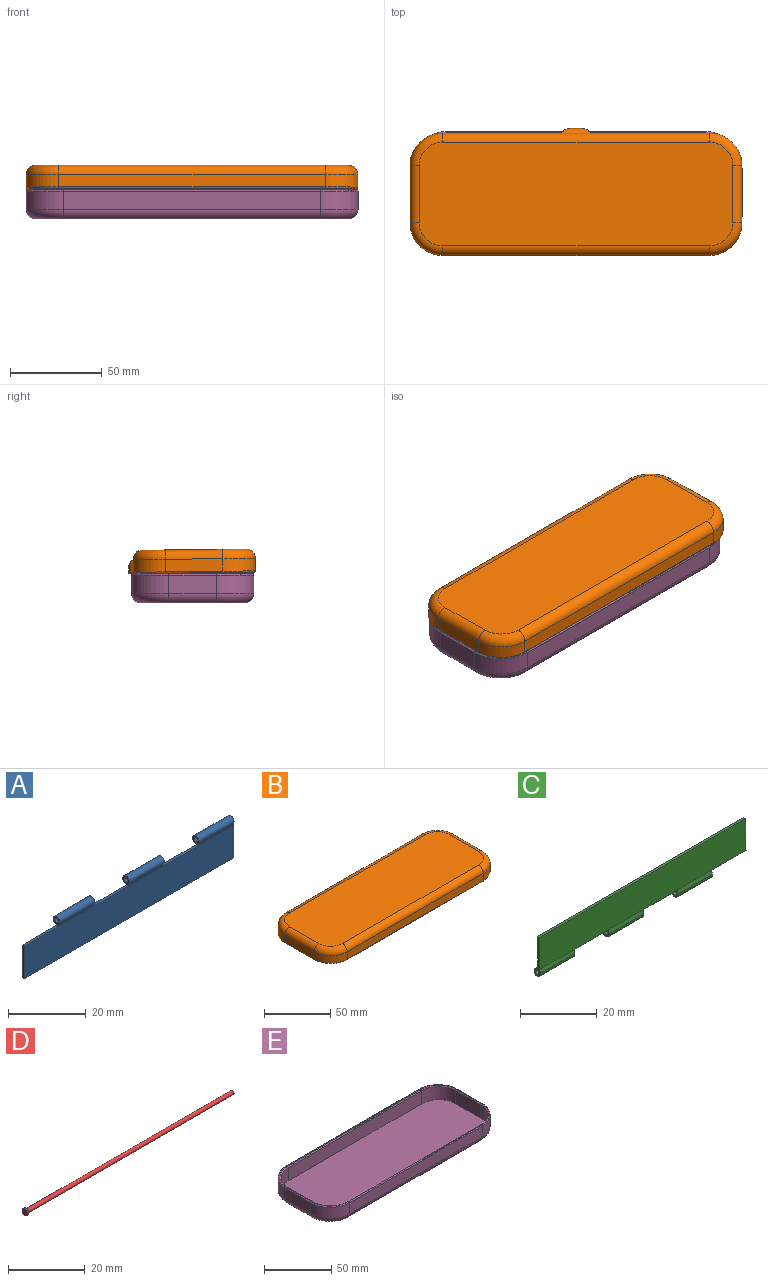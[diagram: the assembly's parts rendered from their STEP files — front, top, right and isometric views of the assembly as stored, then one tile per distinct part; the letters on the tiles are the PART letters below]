
ASSEMBLY  parts=5 mates=5
PART A: 25 faces, bbox 76.2x2.4x12.8 mm
  f0: cylinder r=1.21mm len=12.7mm, axis (-1,0,0), area 78.6mm2, adj f2,f6,f15,f16
  f1: cylinder r=1.21mm len=12.7mm, axis (-1,0,0), area 78.6mm2, adj f3,f5,f17,f18
  f2: plane 12.7x0.24mm, normal (0,0.94,0.33), area 3.3mm2, adj f0,f10,f15,f16
  f3: plane 12.7x0.24mm, normal (0,0.94,0.33), area 3.3mm2, adj f1,f10,f17,f18
  f4: plane 10.16x0.76mm, normal (-1,0,0), area 7.8mm2, adj f10,f11,f19,f24
  f5: plane 12.7x1.18mm, normal (0,-0.98,-0.2), area 15.3mm2, adj f1,f11,f17,f18
  f6: plane 12.7x1.18mm, normal (0,-0.98,-0.2), area 15.3mm2, adj f0,f11,f15,f16
  f7: plane 12.7x1.18mm, normal (0,-0.98,-0.2), area 15.3mm2, adj f8,f11,f13,f14
  f8: cylinder r=1.21mm len=12.7mm, axis (-1,0,0), area 78.6mm2, adj f7,f9,f13,f14
  f9: plane 12.7x0.24mm, normal (0,0.94,0.33), area 3.3mm2, adj f8,f10,f13,f14
  f10: plane 76.2x10.16mm, normal (0,1,0), area 774.2mm2, adj f2,f3,f4,f9,f13,f19,f20,f21
  f11: plane 76.2x10.16mm, normal (0,-1,0), area 774.2mm2, adj f4,f5,f6,f7,f13,f19,f20,f21
  f12: cylinder r=0.64mm len=12.7mm, axis (-1,0,0), area 50.7mm2, adj f13,f14
  f13: plane 12.79x2.41mm, normal (1,0,0), area 11.4mm2, adj f7,f8,f9,f10,f11,f12,f24
  f14: plane 2.63x2.41mm, normal (-1,0,0), area 3.7mm2, adj f7,f8,f9,f12,f21
  f15: plane 2.63x2.41mm, normal (1,0,0), area 3.7mm2, adj f0,f2,f6,f21,f23
  f16: plane 2.63x2.41mm, normal (-1,0,0), area 3.7mm2, adj f0,f2,f6,f20,f23
  f17: plane 2.63x2.41mm, normal (1,0,0), area 3.7mm2, adj f1,f3,f5,f20,f22
  f18: plane 2.63x2.41mm, normal (-1,0,0), area 3.7mm2, adj f1,f3,f5,f19,f22
  f19: plane 12.7x0.76mm, normal (0,0,1), area 9.7mm2, adj f4,f10,f11,f18
  f20: plane 12.7x0.76mm, normal (0,0,1), area 9.7mm2, adj f10,f11,f16,f17
  f21: plane 12.7x0.76mm, normal (0,0,1), area 9.7mm2, adj f10,f11,f14,f15
  f22: cylinder r=0.64mm len=12.7mm, axis (-1,0,0), area 50.7mm2, adj f17,f18
  f23: cylinder r=0.64mm len=12.7mm, axis (-1,0,0), area 50.7mm2, adj f15,f16
  f24: plane 76.2x0.76mm, normal (0,0,-1), area 58.3mm2, adj f4,f10,f11,f13
PART B: 49 faces, bbox 183.9x70.7x12.7 mm
  f0: plane 64.98x6.86mm, normal (0,1,0), area 445.6mm2, adj f10,f18,f31,f40
  f1: plane 179.45x68.45mm, normal (0,0,-1), area 389.2mm2, adj f28,f29,f31,f32,f33,f34,f35,f36
  f2: plane 31.12x6.86mm, normal (-1,0,0), area 213.4mm2, adj f7,f10,f14,f38
  f3: plane 145.42x6.86mm, normal (0,-1,0), area 997.3mm2, adj f7,f8,f11,f36
  f4: plane 31.12x6.86mm, normal (1,0,0), area 213.4mm2, adj f8,f9,f15,f34
  f5: plane 64.98x6.86mm, normal (0,1,0), area 445.6mm2, adj f9,f18,f29,f32
  f6: plane 170.82x56.52mm, normal (0,0,1), area 9515.2mm2, adj f11,f12,f13,f14,f15,f16,f17,f18
  f7: cylinder r=17.78mm len=17.78mm, axis (0,0,1), area 191.5mm2, adj f2,f3,f12,f37
  f8: cylinder r=17.78mm len=17.78mm, axis (0,0,-1), area 191.5mm2, adj f3,f4,f13,f35
  f9: cylinder r=17.78mm len=17.78mm, axis (0,0,1), area 191.5mm2, adj f4,f5,f17,f33
  f10: cylinder r=17.78mm len=17.78mm, axis (0,0,-1), area 191.5mm2, adj f0,f2,f16,f39
  f11: cylinder r=5.08mm len=145.42mm, axis (-1,0,0), area 1160.4mm2, adj f3,f6,f12,f13
  f12: torus R=12.7mm, axis (0,0,1), area 199.7mm2, adj f6,f7,f11,f14
  f13: torus R=12.7mm, axis (0,0,1), area 199.7mm2, adj f6,f8,f11,f15
  f14: cylinder r=5.08mm len=31.12mm, axis (0,1,0), area 248.3mm2, adj f2,f6,f12,f16
  f15: cylinder r=5.08mm len=31.12mm, axis (0,-1,0), area 248.3mm2, adj f4,f6,f13,f17
  f16: torus R=12.7mm, axis (0,0,1), area 199.7mm2, adj f6,f10,f14,f18
  f17: torus R=12.7mm, axis (0,0,1), area 199.7mm2, adj f6,f9,f15,f18
  f18: cylinder r=5.08mm len=145.42mm, axis (1,0,0), area 1160.4mm2, adj f0,f5,f6,f16,f17,f30
  f19: plane 145.42x9.4mm, normal (0,1,0), area 1366.6mm2, adj f21,f24,f27,f43
  f20: plane 145.42x9.4mm, normal (0,-1,0), area 1366.6mm2, adj f21,f23,f26,f46
  f21: plane 176.51x62.11mm, normal (0,0,-1), area 10753.3mm2, adj f19,f20,f22,f23,f24,f25,f26,f27
  f22: plane 31.12x9.4mm, normal (-1,0,0), area 292.4mm2, adj f21,f23,f24,f47
  f23: cylinder r=15.5mm len=15.49mm, axis (0,0,-1), area 226.6mm2, adj f20,f21,f22,f48
  f24: cylinder r=15.5mm len=15.49mm, axis (0,0,-1), area 226.6mm2, adj f19,f21,f22,f45
  f25: plane 31.12x9.4mm, normal (1,0,0), area 292.4mm2, adj f21,f26,f27,f42
  f26: cylinder r=15.5mm len=15.82mm, axis (0,0,-1), area 231.8mm2, adj f20,f21,f25,f44
  f27: cylinder r=15.83mm len=15.82mm, axis (0,0,-1), area 230.5mm2, adj f19,f21,f25,f41
  f28: plane 6.66x3.22mm, normal (0,1,0), area 21.5mm2, adj f1,f29,f30,f31
  f29: cylinder r=5.08mm len=7.62mm, axis (0,0,1), area 30.2mm2, adj f1,f5,f28,f30,f32
  f30: cylinder r=5.08mm len=15.46mm, axis (1,0,0), area 61.3mm2, adj f18,f28,f29,f31
  f31: cylinder r=5.08mm len=7.62mm, axis (0,0,1), area 30.2mm2, adj f0,f1,f28,f30,f40
  f32: cylinder r=0.76mm len=64.98mm, axis (-1,0,0), area 77.6mm2, adj f1,f5,f29,f33
  f33: torus R=17.02mm, axis (0,0,1), area 32.9mm2, adj f1,f9,f32,f34
  f34: cylinder r=0.76mm len=31.12mm, axis (0,1,0), area 37.2mm2, adj f1,f4,f33,f35
  f35: torus R=17.02mm, axis (0,0,1), area 32.9mm2, adj f1,f8,f34,f36
  f36: cylinder r=0.76mm len=145.42mm, axis (1,0,0), area 174.1mm2, adj f1,f3,f35,f37
  f37: torus R=17.02mm, axis (0,0,1), area 32.9mm2, adj f1,f7,f36,f38
  f38: cylinder r=0.76mm len=31.12mm, axis (0,-1,0), area 37.2mm2, adj f1,f2,f37,f39
  f39: torus R=17.02mm, axis (0,0,1), area 32.9mm2, adj f1,f10,f38,f40
  f40: cylinder r=0.76mm len=64.98mm, axis (-1,0,0), area 77.6mm2, adj f0,f1,f31,f39
  f41: torus R=16.59mm, axis (0,0,1), area 29.9mm2, adj f1,f27,f42,f43
  f42: cylinder r=0.76mm len=31.12mm, axis (0,1,0), area 37.2mm2, adj f1,f25,f41,f44
  f43: cylinder r=0.76mm len=145.42mm, axis (-1,0,0), area 174.1mm2, adj f1,f19,f41,f45
  f44: torus R=16.26mm, axis (0,0,1), area 30.1mm2, adj f1,f26,f42,f46
  f45: torus R=16.26mm, axis (0,0,1), area 29.4mm2, adj f1,f24,f43,f47
  f46: cylinder r=0.76mm len=145.42mm, axis (1,0,0), area 174.1mm2, adj f1,f20,f44,f48
  f47: cylinder r=0.76mm len=31.12mm, axis (0,-1,0), area 37.2mm2, adj f1,f22,f45,f48
  f48: torus R=16.26mm, axis (0,0,1), area 29.4mm2, adj f1,f23,f46,f47
PART C: 23 faces, bbox 76.2x2.4x12.8 mm
  f0: plane 76.2x10.16mm, normal (0,-1,0), area 774.2mm2, adj f6,f7,f9,f13,f21,f22
  f1: cylinder r=1.21mm len=12.7mm, axis (-1,0,0), area 78.6mm2, adj f2,f7,f17,f20
  f2: plane 50.8x0.24mm, normal (0,0.94,-0.33), area 7.1mm2, adj f1,f4,f9,f11,f14,f15,f16,f17
  f3: cylinder r=0.64mm len=12.7mm, axis (-1,0,0), area 50.7mm2, adj f17,f20
  f4: cylinder r=1.21mm len=12.7mm, axis (-1,0,0), area 78.6mm2, adj f2,f7,f14,f18
  f5: cylinder r=0.64mm len=12.7mm, axis (-1,0,0), area 50.7mm2, adj f14,f18
  f6: plane 12.7x1.18mm, normal (0,-0.98,0.2), area 15.3mm2, adj f0,f8,f13,f19
  f7: plane 50.8x1.18mm, normal (0,-0.98,0.2), area 31.1mm2, adj f0,f1,f4,f9,f14,f15,f16,f17
  f8: cylinder r=1.21mm len=12.7mm, axis (-1,0,0), area 78.6mm2, adj f6,f10,f13,f19
  f9: plane 10.19x0.77mm, normal (1,0,0), area 7.8mm2, adj f0,f2,f7,f11,f15,f22
  f10: plane 12.7x0.24mm, normal (0,0.94,-0.33), area 3.3mm2, adj f8,f11,f13,f19
  f11: plane 76.2x10.16mm, normal (0,1,0), area 774.2mm2, adj f2,f9,f10,f13,f21,f22
  f12: cylinder r=0.64mm len=12.7mm, axis (-1,0,0), area 50.7mm2, adj f13,f19
  f13: plane 12.79x2.41mm, normal (-1,0,0), area 11.4mm2, adj f0,f6,f8,f10,f11,f12,f22
  f14: plane 2.6x2.41mm, normal (1,0,0), area 3.6mm2, adj f2,f4,f5,f7,f15
  f15: plane 12.7x0.76mm, normal (0,0,-1), area 9.7mm2, adj f2,f7,f9,f14
  f16: plane 12.7x0.76mm, normal (0,0,-1), area 9.7mm2, adj f2,f7,f17,f18
  f17: plane 2.61x2.41mm, normal (1,0,0), area 3.6mm2, adj f1,f2,f3,f7,f16
  f18: plane 2.61x2.41mm, normal (-1,0,0), area 3.6mm2, adj f2,f4,f5,f7,f16
  f19: plane 2.63x2.41mm, normal (1,0,0), area 3.7mm2, adj f6,f8,f10,f12,f21
  f20: plane 2.63x2.41mm, normal (-1,0,0), area 3.7mm2, adj f1,f2,f3,f7,f21
  f21: plane 12.7x0.76mm, normal (0,0,-1), area 9.7mm2, adj f0,f11,f19,f20
  f22: plane 76.2x0.76mm, normal (0,0,1), area 58.3mm2, adj f0,f9,f11,f13
PART D: 5 faces, bbox 76.7x2x2 mm
  f0: cylinder r=0.62mm len=76.2mm, axis (-1,0,0), area 295.2mm2, adj f1,f4
  f1: plane 1.23x1.23mm, normal (1,0,0), area 1.2mm2, adj f0
  f2: cylinder r=1.02mm len=2.04mm, axis (1,0,0), area 3.2mm2, adj f3,f4
  f3: plane 2.04x2.04mm, normal (-1,0,0), area 3.3mm2, adj f2
  f4: plane 2.04x2.04mm, normal (1,0,0), area 2.1mm2, adj f0,f2
PART E: 43 faces, bbox 184.3x70x15.9 mm
  f0: plane 179.45x63.7mm, normal (0,0,1), area 190.2mm2, adj f27,f28,f29,f30,f31,f33,f34,f35
  f1: plane 26.04x10.03mm, normal (-1,0,0), area 261.2mm2, adj f6,f9,f13,f30
  f2: plane 140.34x10.03mm, normal (0,-1,0), area 1408mm2, adj f6,f7,f17,f32
  f3: plane 26.04x10.03mm, normal (1,0,0), area 261.2mm2, adj f7,f8,f14,f31
  f4: plane 140.34x10.03mm, normal (0,1,0), area 1408mm2, adj f8,f9,f10,f27
  f5: plane 170.82x56.52mm, normal (0,0,-1), area 9454.2mm2, adj f10,f11,f12,f13,f14,f15,f16,f17
  f6: cylinder r=20.32mm len=20.32mm, axis (0,0,1), area 320.2mm2, adj f1,f2,f15,f33
  f7: cylinder r=20.32mm len=20.32mm, axis (0,0,-1), area 320.2mm2, adj f2,f3,f16,f35
  f8: cylinder r=20.32mm len=20.32mm, axis (0,0,1), area 320.2mm2, adj f3,f4,f12,f29
  f9: cylinder r=20.32mm len=20.32mm, axis (0,0,-1), area 320.2mm2, adj f1,f4,f11,f28
  f10: cylinder r=5.08mm len=140.34mm, axis (-1,0,0), area 1119.8mm2, adj f4,f5,f11,f12
  f11: torus R=15.24mm, axis (0,0,1), area 231.6mm2, adj f5,f9,f10,f13
  f12: torus R=15.24mm, axis (0,0,1), area 231.6mm2, adj f5,f8,f10,f14
  f13: cylinder r=5.08mm len=26.04mm, axis (0,-1,0), area 207.8mm2, adj f1,f5,f11,f15
  f14: cylinder r=5.08mm len=26.04mm, axis (0,1,0), area 207.8mm2, adj f3,f5,f12,f16
  f15: torus R=15.24mm, axis (0,0,1), area 231.6mm2, adj f5,f6,f13,f17
  f16: torus R=15.24mm, axis (0,0,1), area 231.6mm2, adj f5,f7,f14,f17
  f17: cylinder r=5.08mm len=140.34mm, axis (1,0,0), area 1119.8mm2, adj f2,f5,f15,f16
  f18: plane 26.04x11.94mm, normal (1,0,0), area 310.8mm2, adj f22,f24,f25,f37
  f19: plane 140.34x11.94mm, normal (0,1,0), area 1675.3mm2, adj f22,f23,f24,f36
  f20: plane 26.04x11.94mm, normal (-1,0,0), area 310.8mm2, adj f22,f23,f26,f40
  f21: plane 140.34x11.94mm, normal (0,-1,0), area 1675.3mm2, adj f22,f25,f26,f41
  f22: plane 177.34x62.9mm, normal (0,0,1), area 10856.9mm2, adj f18,f19,f20,f21,f23,f24,f25,f26
  f23: cylinder r=18.99mm len=18.98mm, axis (0,0,1), area 350.2mm2, adj f19,f20,f22,f38
  f24: cylinder r=18.99mm len=18.98mm, axis (0,0,1), area 350.4mm2, adj f18,f19,f22,f34
  f25: cylinder r=18.53mm len=18.52mm, axis (0,0,1), area 339.6mm2, adj f18,f21,f22,f39
  f26: cylinder r=17.88mm len=18.49mm, axis (0,0,1), area 342.6mm2, adj f20,f21,f22,f42
  f27: cylinder r=0.76mm len=140.34mm, axis (1,0,0), area 168mm2, adj f0,f4,f28,f29
  f28: torus R=19.56mm, axis (0,0,1), area 37.7mm2, adj f0,f9,f27,f30
  f29: torus R=19.56mm, axis (0,0,1), area 37.7mm2, adj f0,f8,f27,f31
  f30: cylinder r=0.76mm len=26.04mm, axis (0,1,0), area 31.2mm2, adj f0,f1,f28,f33
  f31: cylinder r=0.76mm len=26.04mm, axis (0,-1,0), area 31.2mm2, adj f0,f3,f29,f35
  f32: cylinder r=0.76mm len=140.34mm, axis (-1,0,0), area 154.8mm2, adj f2,f33,f35,f36
  f33: torus R=19.56mm, axis (0,0,1), area 37.3mm2, adj f0,f6,f30,f32,f34,f36
  f34: torus R=19.75mm, axis (0,0,1), area 35.3mm2, adj f0,f24,f33,f36,f37
  f35: torus R=19.56mm, axis (0,0,1), area 37.3mm2, adj f0,f7,f31,f32,f36,f38
  f36: cylinder r=0.76mm len=140.35mm, axis (-1,0,0), area 154.9mm2, adj f19,f32,f33,f34,f35,f38
  f37: cylinder r=0.76mm len=26.05mm, axis (0,1,0), area 31.2mm2, adj f0,f18,f34,f39
  f38: torus R=19.75mm, axis (0,0,1), area 35.3mm2, adj f0,f23,f35,f36,f40
  f39: torus R=19.29mm, axis (0,0,1), area 34.6mm2, adj f0,f25,f37,f41
  f40: cylinder r=0.76mm len=26.04mm, axis (0,-1,0), area 31.2mm2, adj f0,f20,f38,f42
  f41: cylinder r=0.76mm len=140.34mm, axis (1,0,0), area 168mm2, adj f0,f21,f39,f42
  f42: torus R=18.65mm, axis (0,0,1), area 34.9mm2, adj f0,f26,f40,f41
PLACE A rot(axis=(1,0,0),0deg) t=(-35.07,-22.71,63.22)mm
PLACE B rot(axis=(-1,0,0),0.7deg) t=(-35.66,-32.49,63.08)mm
PLACE C rot(axis=(-1,0,0),0.7deg) t=(-35.07,-22.69,63.19)mm
PLACE D rot(axis=(-1,0,0),0.7deg) t=(-35.07,-22.69,63.19)mm
PLACE E t=(-30.59,-31.56,46.31)mm fixed
MATE fastened C.f1 <-> D.f0  axis (-1,0,0) through (-52.85,-25.47,61.96)mm
MATE fastened B.f19 <-> C.f0  axis (0,1,-0.01) through (-14.75,-26.34,68.47)mm
MATE revolute D.f0 <-> A.f0  axis (-1,0,0) through (23.35,-25.47,61.96)mm
MATE revolute C.f1 <-> D.f0  axis (-1,0,0) through (-52.85,-25.47,61.96)mm
MATE fastened A.f11 <-> E.f19  axis (0,-1,0) through (-14.75,-26.41,55.46)mm
